# Revit family: Gira_000930
name_source: partatom
category: Generic Models
revit_build: Autodesk Revit 2017 (Build: 20160225_1515(x64)
units: mm (PartAtom-declared; Revit-internal decimal feet)

## family parameters
Always vertical = Yes
Can host rebar = No
Cut with Voids When Loaded = No
Part Type = Normal
Room Calculation Point = No
Round Connector Dimension = Use Diameter
Shared = No
Work Plane-Based = No

## types (1)
- closure cab.entry 1-g closed WP SM grey
    BIM = https://media.live.bim.site
    BIMSITE_PRODUCT_ID = 471281dc6a3d43a62ca6753009f1ffa3ca06e068
    Colour = Grey
    Cost = 0 $
    Description = Closure cab.entry 1g closed WP SM GY Seal with cable entry 1-gang (closed) grey Notes : - For cables  6 to 13 mm.
    GTIN = 4010337009306
    HAN = 000930
    HeinzeBIM = https://www.heinze.de
    Manufacturer = Gira
    Model = Duct slider
    Suitable for built-up box flush-mounted switching equipment = Yes
    URL = https://www.gira.de

## geometry (parser evidence)
native form markers: Blend x2, Sweep x2
no freeform markers — native parametric forms only
